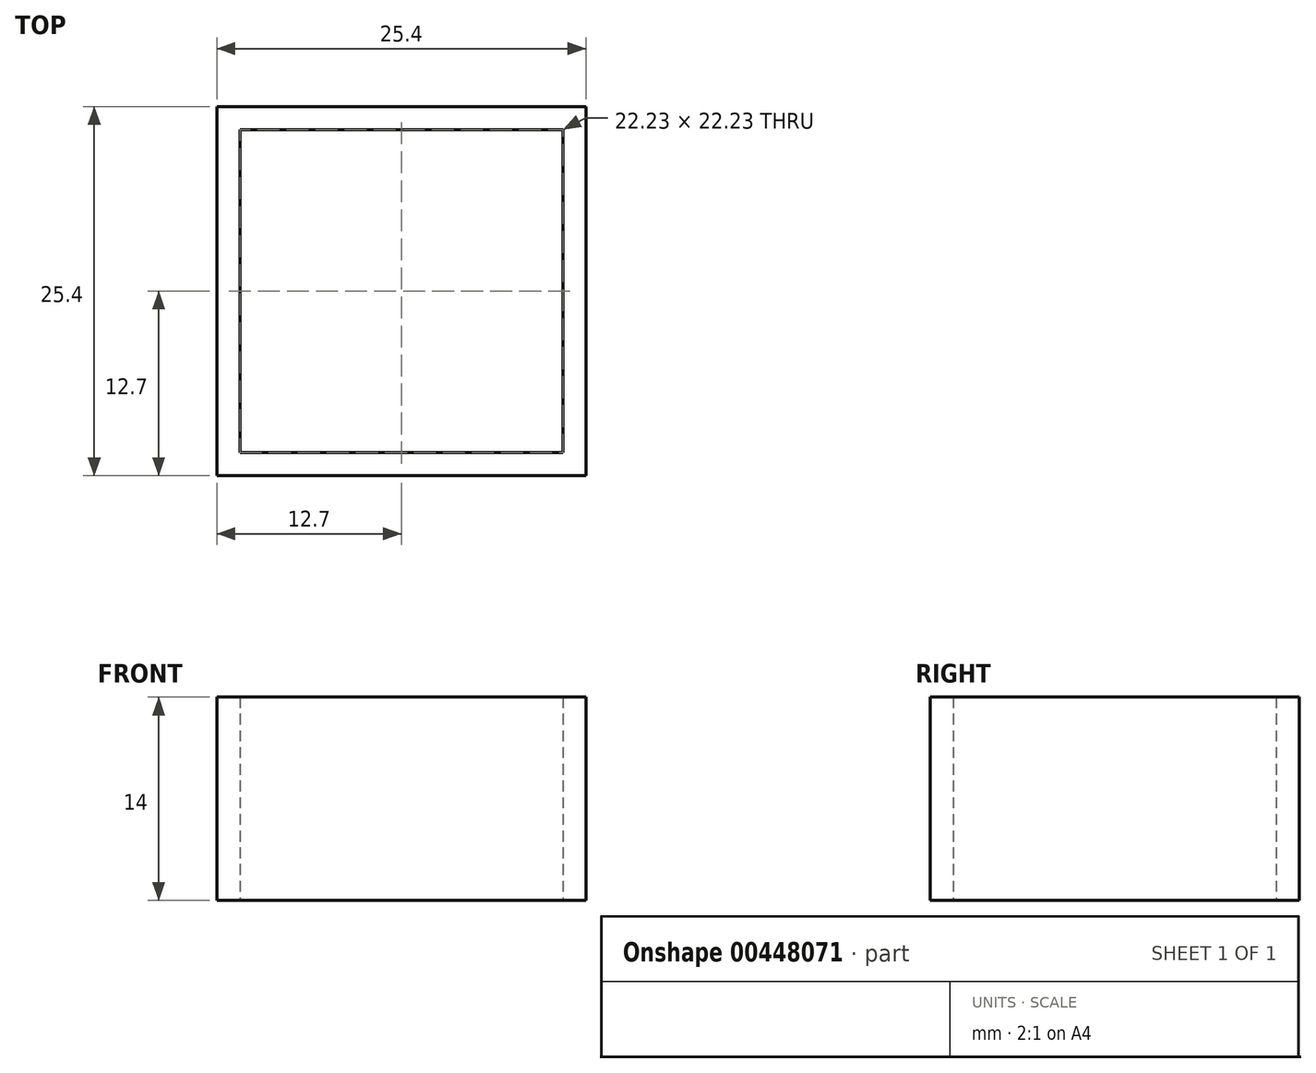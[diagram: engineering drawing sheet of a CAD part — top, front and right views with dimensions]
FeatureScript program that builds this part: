
annotation { "Feature Type Name" : "Feature", "Feature Type Description" : "" }
export const myFeature = defineFeature(function(context is Context, id is Id, definition is map)
    precondition{}
    {
        {
            assignVariable(context, id + "F0", {"name" : "SideH", "anyValue" : 14});
        }
        {
            var Q0;
            Q0=qCreatedBy(makeId("Top.planeOp"),FACE);
            var sketch = newSketch(context, id + "F1", { "sketchPlane" : qUnion([Q0])});
            skLineSegment(sketch, "E0.bottom", {"start": v(-12.7, 12.7) * mm, "end": v(12.7, 12.7) * mm});
            skLineSegment(sketch, "E0.top", {"start": v(-12.7, -12.7) * mm, "end": v(12.7, -12.7) * mm});
            skLineSegment(sketch, "E0.left", {"start": v(-12.7, 12.7) * mm, "end": v(-12.7, -12.7) * mm});
            skLineSegment(sketch, "E0.right", {"start": v(12.7, 12.7) * mm, "end": v(12.7, -12.7) * mm});
            skPoint(sketch, "E0.middle", {"position": v(0, 0) * mm});
            skSolve(sketch);
        }
        {
            var Q0;
            Q0=makeQuery(id+"F1.imprint","IMPRINT",FACE,{"disambiguationData":[TD([[makeQuery(id+"F1.imprint","IMPRINT",EDGE,{"derivedFrom":sQuery(id+"F1.wireOp",EDGE,"E0.bottom")}),-1.0]])]});
            var Q1;
            Q1=qConstructionFilter(qBodyType(qCreatedBy(id+"F1",EDGE),BodyType.WIRE),ConstructionObject.NO);
            extrude(context, id + "F2", {"entities" : qUnion([Q0]), "surfaceEntities" : qUnion([Q1]), "depth" : (getVariable(context, 'SideH')) * mm});
        }
        {
            var Q0;
            Q0=makeQuery(id+"F2.opExtrude","CAP_FACE",FACE,{"disambiguationData":[OSD([sQuery(id+"F1.wireOp",EDGE,"E0.bottom"),sQuery(id+"F1.wireOp",EDGE,"E0.top"),sQuery(id+"F1.wireOp",EDGE,"E0.left"),sQuery(id+"F1.wireOp",EDGE,"E0.right")])],"isStart":false});
            shell(context, id + "F3", {"entities" : qUnion([Q0]), "thickness" : 1.59 * mm});
        }
        {
            var Q0;
            Q0=makeQuery(id+"F3.opShell","OFFSET_FACE",FACE,{"disambiguationData":[OSD([sQuery(id+"F1.wireOp",EDGE,"E0.bottom"),sQuery(id+"F1.wireOp",EDGE,"E0.top"),sQuery(id+"F1.wireOp",EDGE,"E0.left"),sQuery(id+"F1.wireOp",EDGE,"E0.right")])]});
            extrude(context, id + "F4", {"entities" : qUnion([Q0]), "operationType" : NewBodyOperationType.REMOVE, "endBound" : BoundingType.THROUGH_ALL, "oppositeDirection" : true, "depth" : 25.4 * mm});
        }
        {
            var Q0;
            Q0=makeQuery(id+"F2.opExtrude","SWEPT_FACE",FACE,{"disambiguationData":[OSD([sQuery(id+"F1.wireOp",EDGE,"E0.top")])]});
            var sketch = newSketch(context, id + "F5", { "sketchPlane" : qUnion([Q0])});
            skCircle(sketch, "E1", {"center": v(0, 152.4) * mm, "radius": 6.35 * mm});
            skPoint(sketch, "E1.centerSnap0", {"position": v(0, 0) * mm});
            skSolve(sketch);
        }
        {
            var Q0;
            Q0=makeQuery(id+"F5.imprint","IMPRINT",FACE,{"disambiguationData":[TD([[makeQuery(id+"F5.imprint","IMPRINT",EDGE,{"derivedFrom":sQuery(id+"F5.wireOp",EDGE,"E1")}),1.0]])]});
            extrude(context, id + "F6", {"entities" : qUnion([Q0]), "operationType" : NewBodyOperationType.REMOVE, "endBound" : BoundingType.THROUGH_ALL, "oppositeDirection" : true, "depth" : 25.4 * mm});
        }
    });
